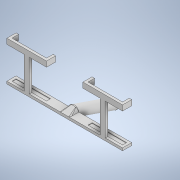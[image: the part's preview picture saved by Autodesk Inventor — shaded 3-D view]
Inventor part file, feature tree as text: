
AUTODESK INVENTOR PART (.ipt)
format: ipt  version: 2020 (Build 240168000, 168)  size: 353,280 bytes
history: native  units: in
note: dims shown in document units (in); Inventor stores cm internally (conversion verified against a paired STEP export)
features: sketch x8, projected_geometry x5, extrude x4, loft x2, other x2, plane x1, sweep x1, fillet x1
ambient origin geometry x8: Origin, YZ Plane, XZ Plane, XY Plane, X Axis, Y Axis, Z Axis, Center Point
bodies: Solid1 (feature_tree)
feature tree (24):
  extrude  "Extrusion1"  Depth=2.6811in
  extrude  "Extrusion2"  Depth=2.6811in
  extrude  "Extrusion3"  Depth=0.1969in
  extrude  "Extrusion4"  Depth=5.9055in
  sketch  "Sketch9"  dims[d15=0.0394in d16=0.0in d17=0.3937in]
  plane  "Work Plane2"
  sweep  "Sweep2"
  loft  "Loft1"
  loft  "Loft2"
  fillet  "Fillet2"  Radius=0.1969in
  sketch  "Sketch2"  dims[d0=0.1969in d1=0.0in d6=2.6811in]
  sketch  "Sketch6"  dims[d7=0.315in d8=2.6811in d9=0.315in d10=0.1969in]
  sketch  "Sketch7"  dims[d11=0.1969in d12=0.1969in]
  projected_geometry  "Projected Loop2"
  projected_geometry  "Projected Loop3"
  projected_geometry  "Projected Loop4"
  sketch  "Sketch8"  dims[d13=0.1969in d14=5.9055in]
  projected_geometry  "Projected Loop5"
  projected_geometry  "Projected Loop6"
  sketch  "Sketch10"  dims[d19=0.3937in d20=2.4769in d21=0.0in]
  sketch  "Sketch11"  dims[d22=0.1969in d23=0.4144in d24=0.0in d25=0.1969in]
  other  "Edges1"
  sketch  "Sketch12"  dims[d27=0.7874in d28=0.0in d29=0.0in d30=0.0in d31=90.0deg d32=0.0in d33=90.0deg d34=0.0in d35=90.0deg d36=0.0in d37=90.0deg d38=0.125in]
  other  "Edges2"
